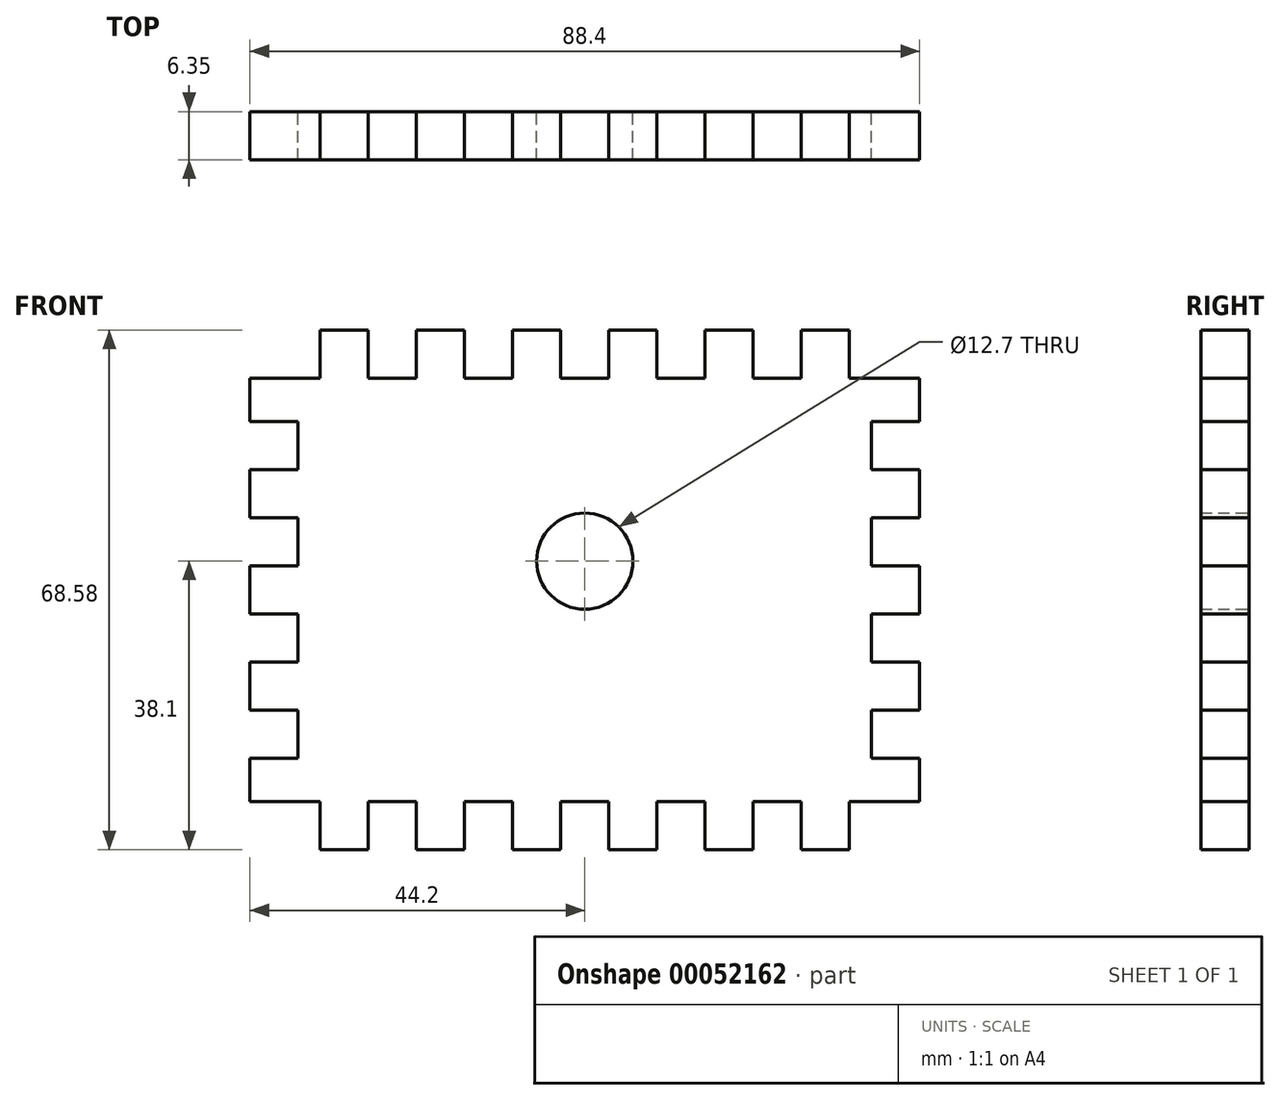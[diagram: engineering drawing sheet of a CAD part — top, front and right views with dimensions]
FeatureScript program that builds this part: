
annotation { "Feature Type Name" : "Feature", "Feature Type Description" : "" }
export const myFeature = defineFeature(function(context is Context, id is Id, definition is map)
    precondition{}
    {
        {
            var Q0;
            Q0=qCreatedBy(makeId("Front.planeOp"),FACE);
            var sketch = newSketch(context, id + "F0", { "sketchPlane" : qUnion([Q0])});
            skLineSegment(sketch, "E0.rect.bottom", {"start": v(37.85, 27.94) * mm, "end": v(34.93, 27.94) * mm});
            skLineSegment(sketch, "E0.rect.top", {"start": v(37.85, -27.94) * mm, "end": v(34.93, -27.94) * mm});
            skLineSegment(sketch, "E0.rect.left", {"start": v(37.85, 22.23) * mm, "end": v(37.85, 15.88) * mm});
            skLineSegment(sketch, "E0.rect.right", {"start": v(-37.85, 22.23) * mm, "end": v(-37.85, 15.88) * mm});
            skPoint(sketch, "E0.rect.middle", {"position": v(0, 0) * mm});
            skLineSegment(sketch, "E1.bottom", {"start": v(-37.85, -27.94) * mm, "end": v(-44.2, -27.94) * mm});
            skLineSegment(sketch, "E1.top", {"start": v(-37.85, -22.23) * mm, "end": v(-44.2, -22.23) * mm});
            skLineSegment(sketch, "E1.right", {"start": v(-44.2, -27.94) * mm, "end": v(-44.2, -22.23) * mm});
            skLineSegment(sketch, "E2.bottom", {"start": v(-37.85, -15.88) * mm, "end": v(-44.2, -15.88) * mm});
            skLineSegment(sketch, "E2.top", {"start": v(-37.85, -9.53) * mm, "end": v(-44.2, -9.53) * mm});
            skLineSegment(sketch, "E2.right", {"start": v(-44.2, -15.88) * mm, "end": v(-44.2, -9.53) * mm});
            skLineSegment(sketch, "E3.bottom", {"start": v(-37.85, -3.18) * mm, "end": v(-44.2, -3.18) * mm});
            skLineSegment(sketch, "E3.top", {"start": v(-37.85, 3.17) * mm, "end": v(-44.2, 3.17) * mm});
            skLineSegment(sketch, "E3.right", {"start": v(-44.2, -3.18) * mm, "end": v(-44.2, 3.17) * mm});
            skLineSegment(sketch, "E4.bottom", {"start": v(-37.85, 9.52) * mm, "end": v(-44.2, 9.52) * mm});
            skLineSegment(sketch, "E4.top", {"start": v(-37.85, 15.88) * mm, "end": v(-44.2, 15.88) * mm});
            skLineSegment(sketch, "E4.right", {"start": v(-44.2, 9.52) * mm, "end": v(-44.2, 15.88) * mm});
            skLineSegment(sketch, "E5.bottom", {"start": v(-37.85, 27.94) * mm, "end": v(-44.2, 27.94) * mm});
            skLineSegment(sketch, "E5.top", {"start": v(-37.85, 22.23) * mm, "end": v(-44.2, 22.23) * mm});
            skLineSegment(sketch, "E5.right", {"start": v(-44.2, 27.94) * mm, "end": v(-44.2, 22.23) * mm});
            skLineSegment(sketch, "E6.top", {"start": v(-34.93, 34.29) * mm, "end": v(-28.58, 34.29) * mm});
            skLineSegment(sketch, "E6.left", {"start": v(-34.93, 27.94) * mm, "end": v(-34.93, 34.29) * mm});
            skLineSegment(sketch, "E6.right", {"start": v(-28.58, 27.94) * mm, "end": v(-28.58, 34.29) * mm});
            skLineSegment(sketch, "E7.top", {"start": v(-22.23, 34.29) * mm, "end": v(-15.88, 34.29) * mm});
            skLineSegment(sketch, "E7.left", {"start": v(-22.23, 27.94) * mm, "end": v(-22.23, 34.29) * mm});
            skLineSegment(sketch, "E7.right", {"start": v(-15.88, 27.94) * mm, "end": v(-15.88, 34.29) * mm});
            skLineSegment(sketch, "E8.top", {"start": v(-9.53, 34.29) * mm, "end": v(-3.18, 34.29) * mm});
            skLineSegment(sketch, "E8.left", {"start": v(-9.53, 27.94) * mm, "end": v(-9.53, 34.29) * mm});
            skLineSegment(sketch, "E8.right", {"start": v(-3.18, 27.94) * mm, "end": v(-3.18, 34.29) * mm});
            skLineSegment(sketch, "E9.MirrorCS", {"start": v(3.18, 27.94) * mm, "end": v(3.18, 34.29) * mm});
            skLineSegment(sketch, "E10.MirrorCS", {"start": v(9.53, 27.94) * mm, "end": v(9.53, 34.29) * mm});
            skLineSegment(sketch, "E11.MirrorCS", {"start": v(9.53, 34.29) * mm, "end": v(3.18, 34.29) * mm});
            skLineSegment(sketch, "E12.MirrorCS", {"start": v(22.23, 27.94) * mm, "end": v(22.23, 34.29) * mm});
            skLineSegment(sketch, "E13.MirrorCS", {"start": v(15.88, 27.94) * mm, "end": v(15.88, 34.29) * mm});
            skLineSegment(sketch, "E14.MirrorCS", {"start": v(22.23, 34.29) * mm, "end": v(15.88, 34.29) * mm});
            skLineSegment(sketch, "E15.MirrorCS", {"start": v(28.58, 27.94) * mm, "end": v(28.58, 34.29) * mm});
            skLineSegment(sketch, "E16.MirrorCS", {"start": v(34.93, 34.29) * mm, "end": v(28.58, 34.29) * mm});
            skLineSegment(sketch, "E17.MirrorCS", {"start": v(34.93, 27.94) * mm, "end": v(34.93, 34.29) * mm});
            skLineSegment(sketch, "E18.MirrorCS", {"start": v(37.85, -27.94) * mm, "end": v(44.2, -27.94) * mm});
            skLineSegment(sketch, "E19.MirrorCS", {"start": v(37.85, -22.23) * mm, "end": v(44.2, -22.23) * mm});
            skLineSegment(sketch, "E20.MirrorCS", {"start": v(37.85, -9.53) * mm, "end": v(44.2, -9.53) * mm});
            skLineSegment(sketch, "E21.MirrorCS", {"start": v(37.85, -3.18) * mm, "end": v(44.2, -3.18) * mm});
            skLineSegment(sketch, "E22.MirrorCS", {"start": v(37.85, 3.17) * mm, "end": v(44.2, 3.17) * mm});
            skLineSegment(sketch, "E23.MirrorCS", {"start": v(37.85, 9.52) * mm, "end": v(44.2, 9.52) * mm});
            skLineSegment(sketch, "E24.MirrorCS", {"start": v(37.85, 15.88) * mm, "end": v(44.2, 15.88) * mm});
            skLineSegment(sketch, "E25.MirrorCS", {"start": v(37.85, 22.23) * mm, "end": v(44.2, 22.23) * mm});
            skLineSegment(sketch, "E26.MirrorCS", {"start": v(37.85, 27.94) * mm, "end": v(44.2, 27.94) * mm});
            skLineSegment(sketch, "E27.MirrorCS", {"start": v(44.2, -27.94) * mm, "end": v(44.2, -22.23) * mm});
            skLineSegment(sketch, "E28.MirrorCS", {"start": v(44.2, 9.52) * mm, "end": v(44.2, 15.88) * mm});
            skLineSegment(sketch, "E29.MirrorCS", {"start": v(44.2, -3.18) * mm, "end": v(44.2, 3.17) * mm});
            skLineSegment(sketch, "E30.MirrorCS", {"start": v(44.2, 27.94) * mm, "end": v(44.2, 22.23) * mm});
            skLineSegment(sketch, "E31.MirrorCS", {"start": v(44.2, -15.88) * mm, "end": v(44.2, -9.53) * mm});
            skLineSegment(sketch, "E32.trimOffspring", {"start": v(-37.85, 9.52) * mm, "end": v(-37.85, 3.17) * mm});
            skLineSegment(sketch, "E33.trimOffspring", {"start": v(-37.85, -3.18) * mm, "end": v(-37.85, -9.53) * mm});
            skLineSegment(sketch, "E34.trimOffspring", {"start": v(-37.85, -15.88) * mm, "end": v(-37.85, -22.23) * mm});
            skLineSegment(sketch, "E35.trimOffspring", {"start": v(-34.93, 27.94) * mm, "end": v(-37.85, 27.94) * mm});
            skLineSegment(sketch, "E36.trimOffspring", {"start": v(-22.23, 27.94) * mm, "end": v(-28.58, 27.94) * mm});
            skLineSegment(sketch, "E37.trimOffspring", {"start": v(-9.53, 27.94) * mm, "end": v(-15.88, 27.94) * mm});
            skLineSegment(sketch, "E38.trimOffspring", {"start": v(3.18, 27.94) * mm, "end": v(-3.18, 27.94) * mm});
            skLineSegment(sketch, "E39.trimOffspring", {"start": v(15.88, 27.94) * mm, "end": v(9.53, 27.94) * mm});
            skLineSegment(sketch, "E40.trimOffspring", {"start": v(28.58, 27.94) * mm, "end": v(22.23, 27.94) * mm});
            skLineSegment(sketch, "E41.trimOffspring", {"start": v(37.85, 9.52) * mm, "end": v(37.85, 3.17) * mm});
            skLineSegment(sketch, "E42.trimOffspring", {"start": v(37.85, -3.18) * mm, "end": v(37.85, -9.53) * mm});
            skLineSegment(sketch, "E43", {"start": v(44.2, -15.88) * mm, "end": v(37.85, -15.88) * mm});
            skLineSegment(sketch, "E44.trimOffspring", {"start": v(37.85, -15.88) * mm, "end": v(37.85, -22.23) * mm});
            skLineSegment(sketch, "E45.MirrorCS", {"start": v(22.23, -34.29) * mm, "end": v(15.88, -34.29) * mm});
            skLineSegment(sketch, "E46.MirrorCS", {"start": v(15.88, -27.94) * mm, "end": v(9.53, -27.94) * mm});
            skLineSegment(sketch, "E47.MirrorCS", {"start": v(28.58, -27.94) * mm, "end": v(28.58, -34.29) * mm});
            skLineSegment(sketch, "E48.MirrorCS", {"start": v(-34.93, -34.29) * mm, "end": v(-28.58, -34.29) * mm});
            skLineSegment(sketch, "E49.MirrorCS", {"start": v(-9.53, -27.94) * mm, "end": v(-9.53, -34.29) * mm});
            skLineSegment(sketch, "E50.MirrorCS", {"start": v(-3.18, -27.94) * mm, "end": v(-3.18, -34.29) * mm});
            skLineSegment(sketch, "E51.MirrorCS", {"start": v(22.23, -27.94) * mm, "end": v(22.23, -34.29) * mm});
            skLineSegment(sketch, "E52.MirrorCS", {"start": v(-9.53, -34.29) * mm, "end": v(-3.18, -34.29) * mm});
            skLineSegment(sketch, "E53.MirrorCS", {"start": v(9.53, -27.94) * mm, "end": v(9.53, -34.29) * mm});
            skLineSegment(sketch, "E54.MirrorCS", {"start": v(3.18, -27.94) * mm, "end": v(-3.18, -27.94) * mm});
            skLineSegment(sketch, "E55.MirrorCS", {"start": v(15.88, -27.94) * mm, "end": v(15.88, -34.29) * mm});
            skLineSegment(sketch, "E56.MirrorCS", {"start": v(-34.93, -27.94) * mm, "end": v(-34.93, -34.29) * mm});
            skLineSegment(sketch, "E57.MirrorCS", {"start": v(34.93, -34.29) * mm, "end": v(28.58, -34.29) * mm});
            skLineSegment(sketch, "E58.MirrorCS", {"start": v(-22.23, -27.94) * mm, "end": v(-28.58, -27.94) * mm});
            skLineSegment(sketch, "E59.MirrorCS", {"start": v(-22.23, -27.94) * mm, "end": v(-22.23, -34.29) * mm});
            skLineSegment(sketch, "E60.MirrorCS", {"start": v(34.93, -27.94) * mm, "end": v(34.93, -34.29) * mm});
            skLineSegment(sketch, "E61.MirrorCS", {"start": v(9.53, -34.29) * mm, "end": v(3.18, -34.29) * mm});
            skLineSegment(sketch, "E62.MirrorCS", {"start": v(-15.88, -27.94) * mm, "end": v(-15.88, -34.29) * mm});
            skLineSegment(sketch, "E63.MirrorCS", {"start": v(3.18, -27.94) * mm, "end": v(3.18, -34.29) * mm});
            skLineSegment(sketch, "E64.MirrorCS", {"start": v(28.58, -27.94) * mm, "end": v(22.23, -27.94) * mm});
            skLineSegment(sketch, "E65.MirrorCS", {"start": v(-9.53, -27.94) * mm, "end": v(-15.88, -27.94) * mm});
            skLineSegment(sketch, "E66.MirrorCS", {"start": v(-28.58, -27.94) * mm, "end": v(-28.58, -34.29) * mm});
            skLineSegment(sketch, "E67.MirrorCS", {"start": v(-22.23, -34.29) * mm, "end": v(-15.88, -34.29) * mm});
            skLineSegment(sketch, "E68.trimOffspring", {"start": v(-34.93, -27.94) * mm, "end": v(-37.85, -27.94) * mm});
            skCircle(sketch, "E69", {"center": v(0, 3.81) * mm, "radius": 6.35 * mm});
            skSolve(sketch);
        }
        {
            var Q0;
            Q0=makeQuery(id+"F0.imprint","IMPRINT",FACE,{"disambiguationData":[TD([[makeQuery(id+"F0.imprint","IMPRINT",EDGE,{"derivedFrom":sQuery(id+"F0.wireOp",EDGE,"E0.rect.bottom")}),1.0]])]});
            extrude(context, id + "F1", {"entities" : qUnion([Q0]), "depth" : 6.35 * mm});
        }
    });
